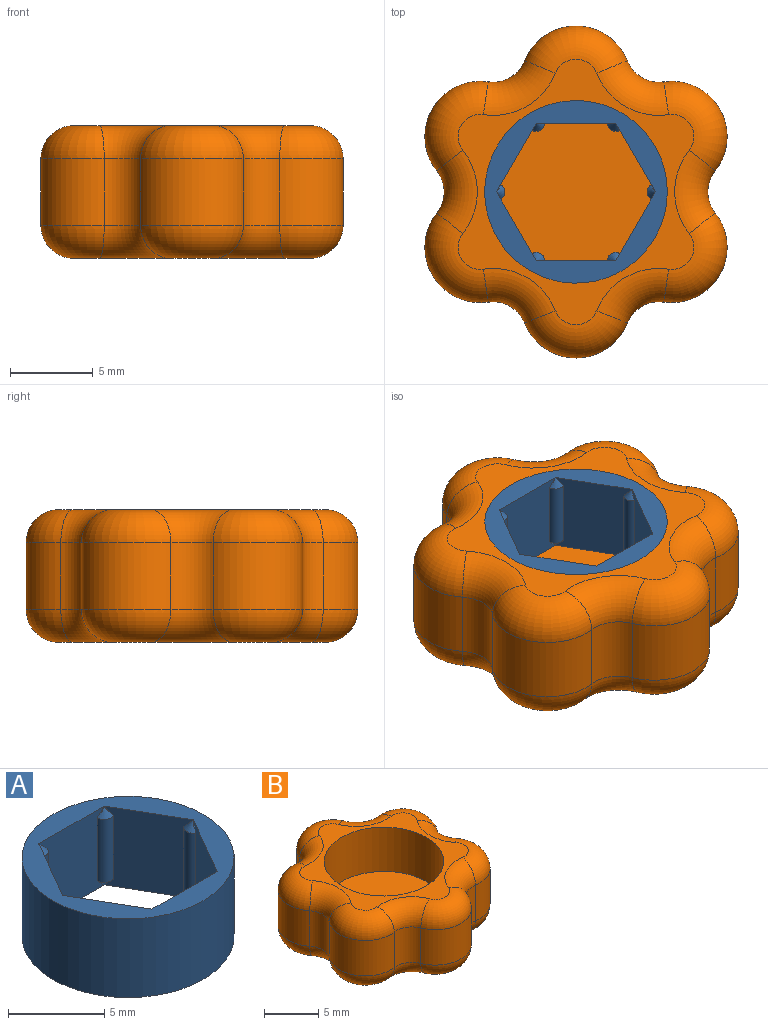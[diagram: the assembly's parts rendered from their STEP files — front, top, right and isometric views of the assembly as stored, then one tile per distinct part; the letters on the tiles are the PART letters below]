
ASSEMBLY  parts=2 mates=1
PART A: 27 faces, bbox 11x11x5 mm
  f0: plane 5x4.15mm, normal (0.87,-0.5,0), area 19.5mm2, adj f7,f8,f21,f22,f23,f24,f25,f26
  f1: plane 5x4.79mm, normal (0,-1,0), area 19.5mm2, adj f7,f8,f9,f10,f11,f21,f22,f23
  f2: plane 5x4.15mm, normal (-0.87,-0.5,0), area 19.5mm2, adj f7,f8,f9,f10,f11,f15,f16,f17
  f3: plane 5x4.15mm, normal (-0.87,0.5,0), area 19.5mm2, adj f7,f8,f12,f13,f14,f15,f16,f17
  f4: plane 5x4.79mm, normal (0,1,0), area 19.5mm2, adj f7,f8,f12,f13,f14,f18,f19,f20
  f5: plane 5x4.15mm, normal (0.87,0.5,0), area 19.5mm2, adj f7,f8,f18,f19,f20,f24,f25,f26
  f6: cylinder r=5.5mm len=11mm, axis (0,0,-1), area 172.8mm2, adj f7,f8
  f7: plane 11x11mm, normal (0,0,1), area 35.4mm2, adj f0,f1,f2,f3,f4,f5,f6
  f8: plane 11x11mm, normal (0,0,-1), area 35.4mm2, adj f0,f1,f2,f3,f4,f5,f6
  f9: cylinder r=0.5mm len=4mm, axis (0,0,-1), area 4.2mm2, adj f1,f2,f10,f11
  f10: cone r=0.5mm half-angle=45deg, axis (0,0,-1), area 0.4mm2, adj f1,f2,f9
  f11: cone r=0.5mm half-angle=45deg, axis (0,0,1), area 0.4mm2, adj f1,f2,f9
  f12: cylinder r=0.5mm len=4mm, axis (0,0,-1), area 4.2mm2, adj f3,f4,f13,f14
  f13: cone r=0.5mm half-angle=45deg, axis (0,0,-1), area 0.4mm2, adj f3,f4,f12
  f14: cone r=0.5mm half-angle=45deg, axis (0,0,1), area 0.4mm2, adj f3,f4,f12
  f15: cylinder r=0.5mm len=4mm, axis (0,0,-1), area 4.2mm2, adj f2,f3,f16,f17
  f16: cone r=0.5mm half-angle=45deg, axis (0,0,-1), area 0.4mm2, adj f2,f3,f15
  f17: cone r=0.5mm half-angle=45deg, axis (0,0,1), area 0.4mm2, adj f2,f3,f15
  f18: cylinder r=0.5mm len=4mm, axis (0,0,-1), area 4.2mm2, adj f4,f5,f19,f20
  f19: cone r=0.5mm half-angle=45deg, axis (0,0,-1), area 0.4mm2, adj f4,f5,f18
  f20: cone r=0.5mm half-angle=45deg, axis (0,0,1), area 0.4mm2, adj f4,f5,f18
  f21: cylinder r=0.5mm len=4mm, axis (0,0,-1), area 4.2mm2, adj f0,f1,f22,f23
  f22: cone r=0.5mm half-angle=45deg, axis (0,0,-1), area 0.4mm2, adj f0,f1,f21
  f23: cone r=0.5mm half-angle=45deg, axis (0,0,1), area 0.4mm2, adj f0,f1,f21
  f24: cylinder r=0.5mm len=4mm, axis (0,0,-1), area 4.2mm2, adj f0,f5,f25,f26
  f25: cone r=0.5mm half-angle=45deg, axis (0,0,-1), area 0.4mm2, adj f0,f5,f24
  f26: cone r=0.5mm half-angle=45deg, axis (0,0,1), area 0.4mm2, adj f0,f5,f24
PART B: 40 faces, bbox 18.2x20x8 mm
  f0: plane 16x14.21mm, normal (0,0,1), area 52mm2, adj f14,f16,f17,f18,f19,f20,f21,f22
  f1: plane 16x14.21mm, normal (0,0,-1), area 147mm2, adj f28,f29,f30,f31,f32,f33,f34,f35
  f2: cylinder r=3.33mm len=6.19mm, axis (0,0,1), area 31.8mm2, adj f3,f6,f19,f36
  f3: cylinder r=2.05mm len=4mm, axis (0,0,1), area 10.9mm2, adj f2,f4,f17,f34
  f4: cylinder r=3.33mm len=5.4mm, axis (0,0,1), area 31.8mm2, adj f3,f13,f16,f32
  f5: cylinder r=3.33mm len=5.4mm, axis (0,0,1), area 31.8mm2, adj f6,f8,f23,f39
  f6: cylinder r=2.05mm len=4mm, axis (0,0,1), area 10.9mm2, adj f2,f5,f21,f38
  f7: cylinder r=3.33mm len=5.4mm, axis (0,0,1), area 31.8mm2, adj f8,f10,f27,f35
  f8: cylinder r=2.05mm len=4mm, axis (0,0,1), area 10.9mm2, adj f5,f7,f25,f37
  f9: cylinder r=3.33mm len=6.19mm, axis (0,0,1), area 31.8mm2, adj f10,f12,f24,f31
  f10: cylinder r=2.05mm len=4mm, axis (0,0,1), area 10.9mm2, adj f7,f9,f26,f33
  f11: cylinder r=3.33mm len=5.4mm, axis (0,0,1), area 31.8mm2, adj f12,f13,f20,f28
  f12: cylinder r=2.05mm len=4mm, axis (0,0,1), area 10.9mm2, adj f9,f11,f22,f29
  f13: cylinder r=2.05mm len=4mm, axis (0,0,1), area 10.9mm2, adj f4,f11,f18,f30
  f14: cylinder r=5.5mm len=11mm, axis (0,0,1), area 172.8mm2, adj f0,f15
  f15: plane 11x11mm, normal (0,0,1), area 95mm2, adj f14
  f16: torus R=1.33mm, axis (0,0,1), area 19.5mm2, adj f0,f4,f17,f18
  f17: torus R=4.05mm, axis (0,0,1), area 11.6mm2, adj f0,f3,f16,f19
  f18: torus R=4.05mm, axis (0,0,1), area 11.6mm2, adj f0,f13,f16,f20
  f19: torus R=1.33mm, axis (0,0,1), area 19.5mm2, adj f0,f2,f17,f21
  f20: torus R=1.33mm, axis (0,0,1), area 19.5mm2, adj f0,f11,f18,f22
  f21: torus R=4.05mm, axis (0,0,1), area 11.6mm2, adj f0,f6,f19,f23
  f22: torus R=4.05mm, axis (0,0,1), area 11.6mm2, adj f0,f12,f20,f24
  f23: torus R=1.33mm, axis (0,0,1), area 19.5mm2, adj f0,f5,f21,f25
  f24: torus R=1.33mm, axis (0,0,1), area 19.5mm2, adj f0,f9,f22,f26
  f25: torus R=4.05mm, axis (0,0,1), area 11.6mm2, adj f0,f8,f23,f27
  f26: torus R=4.05mm, axis (0,0,1), area 11.6mm2, adj f0,f10,f24,f27
  f27: torus R=1.33mm, axis (0,0,1), area 19.5mm2, adj f0,f7,f25,f26
  f28: torus R=1.33mm, axis (0,0,1), area 19.5mm2, adj f1,f11,f29,f30
  f29: torus R=4.05mm, axis (0,0,1), area 11.6mm2, adj f1,f12,f28,f31
  f30: torus R=4.05mm, axis (0,0,1), area 11.6mm2, adj f1,f13,f28,f32
  f31: torus R=1.33mm, axis (0,0,1), area 19.5mm2, adj f1,f9,f29,f33
  f32: torus R=1.33mm, axis (0,0,1), area 19.5mm2, adj f1,f4,f30,f34
  f33: torus R=4.05mm, axis (0,0,1), area 11.6mm2, adj f1,f10,f31,f35
  f34: torus R=4.05mm, axis (0,0,1), area 11.6mm2, adj f1,f3,f32,f36
  f35: torus R=1.33mm, axis (0,0,1), area 19.5mm2, adj f1,f7,f33,f37
  f36: torus R=1.33mm, axis (0,0,1), area 19.5mm2, adj f1,f2,f34,f38
  f37: torus R=4.05mm, axis (0,0,1), area 11.6mm2, adj f1,f8,f35,f39
  f38: torus R=4.05mm, axis (0,0,1), area 11.6mm2, adj f1,f6,f36,f39
  f39: torus R=1.33mm, axis (0,0,1), area 19.5mm2, adj f1,f5,f37,f38
PLACE A t=(7.72,-10.47,7.23)mm
PLACE B t=(7.72,-10.47,4.23)mm
MATE fastened B.f14 <-> A.f6  axis (0,0,1) through (7.72,-10.47,7.23)mm
